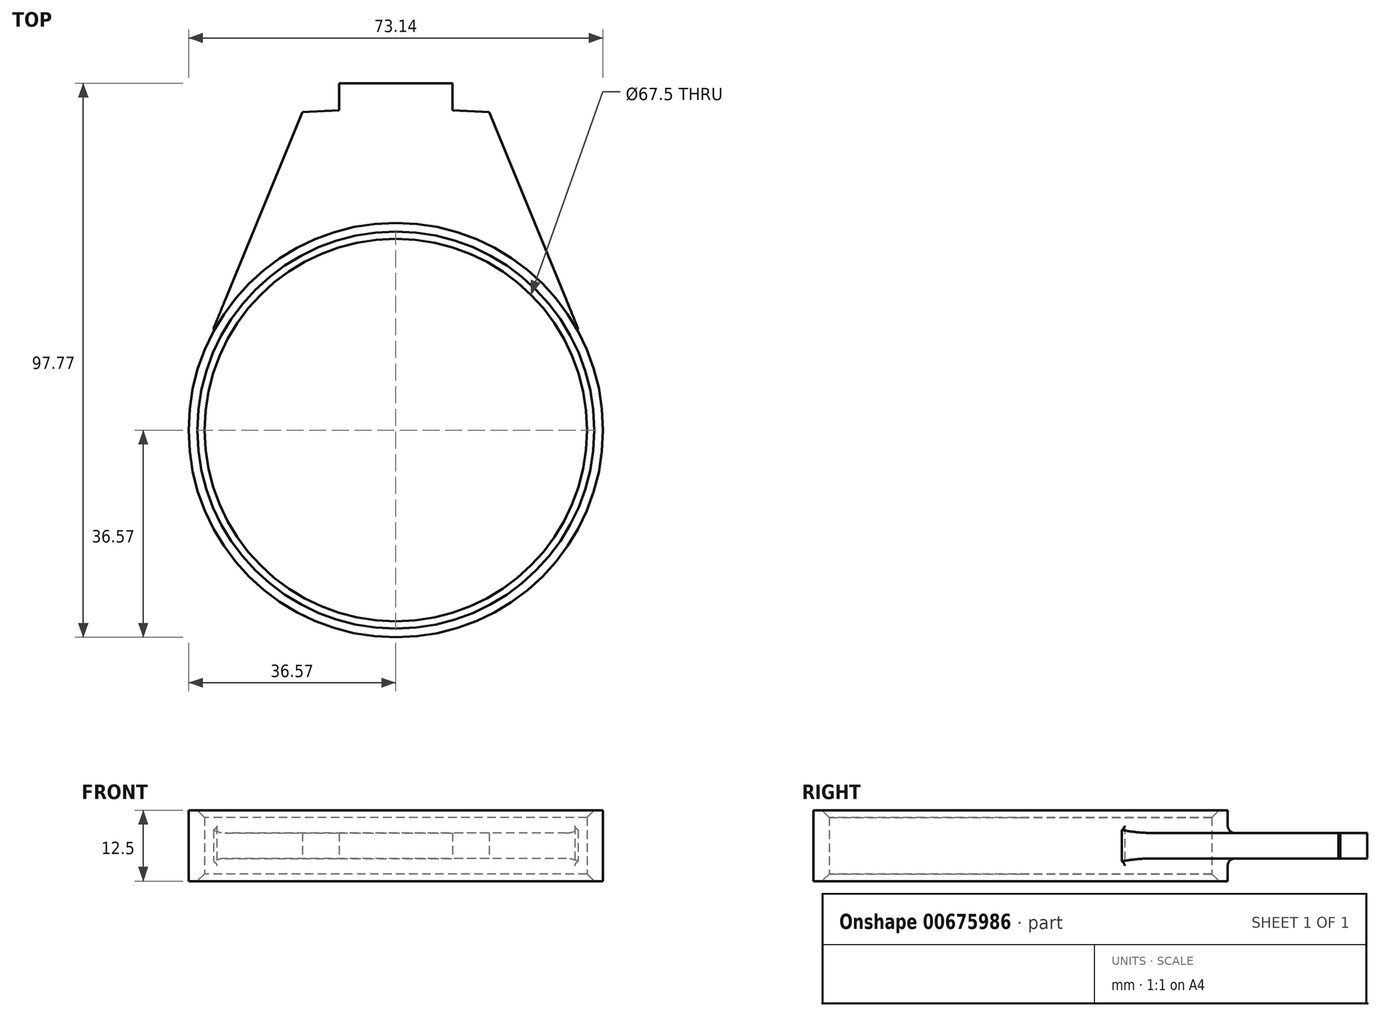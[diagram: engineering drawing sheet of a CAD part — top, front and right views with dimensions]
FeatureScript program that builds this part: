
annotation { "Feature Type Name" : "Feature", "Feature Type Description" : "" }
export const myFeature = defineFeature(function(context is Context, id is Id, definition is map)
    precondition{}
    {
        {
            var Q0;
            Q0=qCreatedBy(makeId("Top.planeOp"),FACE);
            var sketch = newSketch(context, id + "F0", { "sketchPlane" : qUnion([Q0])});
            skCircle(sketch, "E0", {"center": v(0, 0) * mm, "radius": 33.75 * mm});
            skCircle(sketch, "E1", {"center": v(0, 0) * mm, "radius": 36.56 * mm});
            skSolve(sketch);
        }
        {
            var Q0;
            Q0=makeQuery(id+"F0.imprint","IMPRINT",FACE,{"disambiguationData":[TD([[makeQuery(id+"F0.imprint","IMPRINT",EDGE,{"derivedFrom":sQuery(id+"F0.wireOp",EDGE,"E0")}),-1.0]])]});
            extrude(context, id + "F1", {"entities" : qUnion([Q0]), "endBound" : BoundingType.SYMMETRIC, "depth" : 12.5 * mm, "offsetDistance" : 25.4 * mm});
        }
        {
            var Q0;
            Q0=qCreatedBy(makeId("Top.planeOp"),FACE);
            var sketch = newSketch(context, id + "F2", { "sketchPlane" : qUnion([Q0])});
            skLineSegment(sketch, "E2", {"start": v(-32.18, 17.9) * mm, "end": v(-16.5, 56.1) * mm});
            skLineSegment(sketch, "E3", {"start": v(-16.5, 56.1) * mm, "end": v(-10, 56.45) * mm});
            skLineSegment(sketch, "E4", {"start": v(-10, 56.45) * mm, "end": v(-10, 61.2) * mm});
            skLineSegment(sketch, "E5", {"start": v(-10, 61.2) * mm, "end": v(0, 61.2) * mm});
            skLineSegment(sketch, "E6.MirrorCS", {"start": v(32.18, 17.9) * mm, "end": v(16.5, 56.1) * mm});
            skLineSegment(sketch, "E7.MirrorCS", {"start": v(16.5, 56.1) * mm, "end": v(10, 56.45) * mm});
            skLineSegment(sketch, "E8.MirrorCS", {"start": v(10, 56.45) * mm, "end": v(10, 61.2) * mm});
            skLineSegment(sketch, "E9.MirrorCS", {"start": v(10, 61.2) * mm, "end": v(0, 61.2) * mm});
            skLineSegment(sketch, "E10", {"start": v(-32.18, 17.9) * mm, "end": v(-19.61, 28.8) * mm});
            skLineSegment(sketch, "E11", {"start": v(-19.61, 28.8) * mm, "end": v(-8.4, 33.97) * mm});
            skLineSegment(sketch, "E12", {"start": v(-8.4, 33.97) * mm, "end": v(3.7, 35.15) * mm});
            skLineSegment(sketch, "E13", {"start": v(3.7, 35.15) * mm, "end": v(15.64, 31.76) * mm});
            skLineSegment(sketch, "E14", {"start": v(15.64, 31.76) * mm, "end": v(24.5, 24.38) * mm});
            skLineSegment(sketch, "E15", {"start": v(24.5, 24.38) * mm, "end": v(32.18, 17.9) * mm});
            skSolve(sketch);
        }
        {
            var Q0;
            Q0=makeQuery(id+"F2.imprint","IMPRINT",FACE,{"disambiguationData":[TD([[makeQuery(id+"F2.imprint","IMPRINT",EDGE,{"derivedFrom":sQuery(id+"F2.wireOp",EDGE,"E2")}),-1.0]])]});
            extrude(context, id + "F3", {"entities" : qUnion([Q0]), "endBound" : BoundingType.SYMMETRIC, "depth" : 4.5 * mm, "offsetDistance" : 25.4 * mm});
        }
        {
            var Q0;
            Q0=makeQuery(id+"F3.opExtrude","SWEPT_BODY",BODY,{"disambiguationData":[OSD([sQuery(id+"F2.wireOp",EDGE,"E2"),sQuery(id+"F2.wireOp",EDGE,"E3"),sQuery(id+"F2.wireOp",EDGE,"E4"),sQuery(id+"F2.wireOp",EDGE,"E5"),sQuery(id+"F2.wireOp",EDGE,"E6.MirrorCS"),sQuery(id+"F2.wireOp",EDGE,"E7.MirrorCS"),sQuery(id+"F2.wireOp",EDGE,"E8.MirrorCS"),sQuery(id+"F2.wireOp",EDGE,"E9.MirrorCS"),sQuery(id+"F2.wireOp",EDGE,"E10"),sQuery(id+"F2.wireOp",EDGE,"E11"),sQuery(id+"F2.wireOp",EDGE,"E12"),sQuery(id+"F2.wireOp",EDGE,"E13"),sQuery(id+"F2.wireOp",EDGE,"E14"),sQuery(id+"F2.wireOp",EDGE,"E15")])]});
            var Q1;
            Q1=makeQuery(id+"F1.opExtrude","SWEPT_BODY",BODY,{"disambiguationData":[OSD([sQuery(id+"F0.wireOp",EDGE,"E0"),sQuery(id+"F0.wireOp",EDGE,"E1")])]});
            booleanBodies(context, id + "F4", {"operationType" : BooleanOperationType.UNION, "tools" : qUnion([Q0, Q1])});
        }
        {
            var Q0;
            Q0=makeQuery(id+"F4.opBoolean","INTERSECT",EDGE,{"derivedFrom":[makeQuery(id+"F1.opExtrude","SWEPT_FACE",FACE,{"disambiguationData":[OSD([sQuery(id+"F0.wireOp",EDGE,"E1")])]}),makeQuery(id+"F3.opExtrude","CAP_FACE",FACE,{"disambiguationData":[OSD([sQuery(id+"F2.wireOp",EDGE,"E2"),sQuery(id+"F2.wireOp",EDGE,"E3"),sQuery(id+"F2.wireOp",EDGE,"E4"),sQuery(id+"F2.wireOp",EDGE,"E5"),sQuery(id+"F2.wireOp",EDGE,"E6.MirrorCS"),sQuery(id+"F2.wireOp",EDGE,"E7.MirrorCS"),sQuery(id+"F2.wireOp",EDGE,"E8.MirrorCS"),sQuery(id+"F2.wireOp",EDGE,"E9.MirrorCS"),sQuery(id+"F2.wireOp",EDGE,"E10"),sQuery(id+"F2.wireOp",EDGE,"E11"),sQuery(id+"F2.wireOp",EDGE,"E12"),sQuery(id+"F2.wireOp",EDGE,"E13"),sQuery(id+"F2.wireOp",EDGE,"E14"),sQuery(id+"F2.wireOp",EDGE,"E15")])],"isStart":false})]});
            var Q1;
            Q1=makeQuery(id+"F4.opBoolean","INTERSECT",EDGE,{"derivedFrom":[makeQuery(id+"F1.opExtrude","SWEPT_FACE",FACE,{"disambiguationData":[OSD([sQuery(id+"F0.wireOp",EDGE,"E1")])]}),makeQuery(id+"F3.opExtrude","CAP_FACE",FACE,{"disambiguationData":[OSD([sQuery(id+"F2.wireOp",EDGE,"E2"),sQuery(id+"F2.wireOp",EDGE,"E3"),sQuery(id+"F2.wireOp",EDGE,"E4"),sQuery(id+"F2.wireOp",EDGE,"E5"),sQuery(id+"F2.wireOp",EDGE,"E6.MirrorCS"),sQuery(id+"F2.wireOp",EDGE,"E7.MirrorCS"),sQuery(id+"F2.wireOp",EDGE,"E8.MirrorCS"),sQuery(id+"F2.wireOp",EDGE,"E9.MirrorCS"),sQuery(id+"F2.wireOp",EDGE,"E10"),sQuery(id+"F2.wireOp",EDGE,"E11"),sQuery(id+"F2.wireOp",EDGE,"E12"),sQuery(id+"F2.wireOp",EDGE,"E13"),sQuery(id+"F2.wireOp",EDGE,"E14"),sQuery(id+"F2.wireOp",EDGE,"E15")])],"isStart":true})]});
            fillet(context, id + "F5", {"entities" : qUnion([Q0, Q1]), "radius" : 1.27 * mm, "allowEdgeOverflow" : false});
        }
        {
            var Q0;
            Q0=makeQuery(id+"F1.opExtrude","CAP_EDGE",EDGE,{"disambiguationData":[OSD([sQuery(id+"F0.wireOp",EDGE,"E0")])],"isStart":true});
            var Q1;
            Q1=makeQuery(id+"F1.opExtrude","CAP_EDGE",EDGE,{"disambiguationData":[OSD([sQuery(id+"F0.wireOp",EDGE,"E0")])],"isStart":false});
            chamfer(context, id + "F6", {"entities" : qUnion([Q0, Q1]), "width" : 1.27 * mm, "tangentPropagation" : true});
        }
    });
